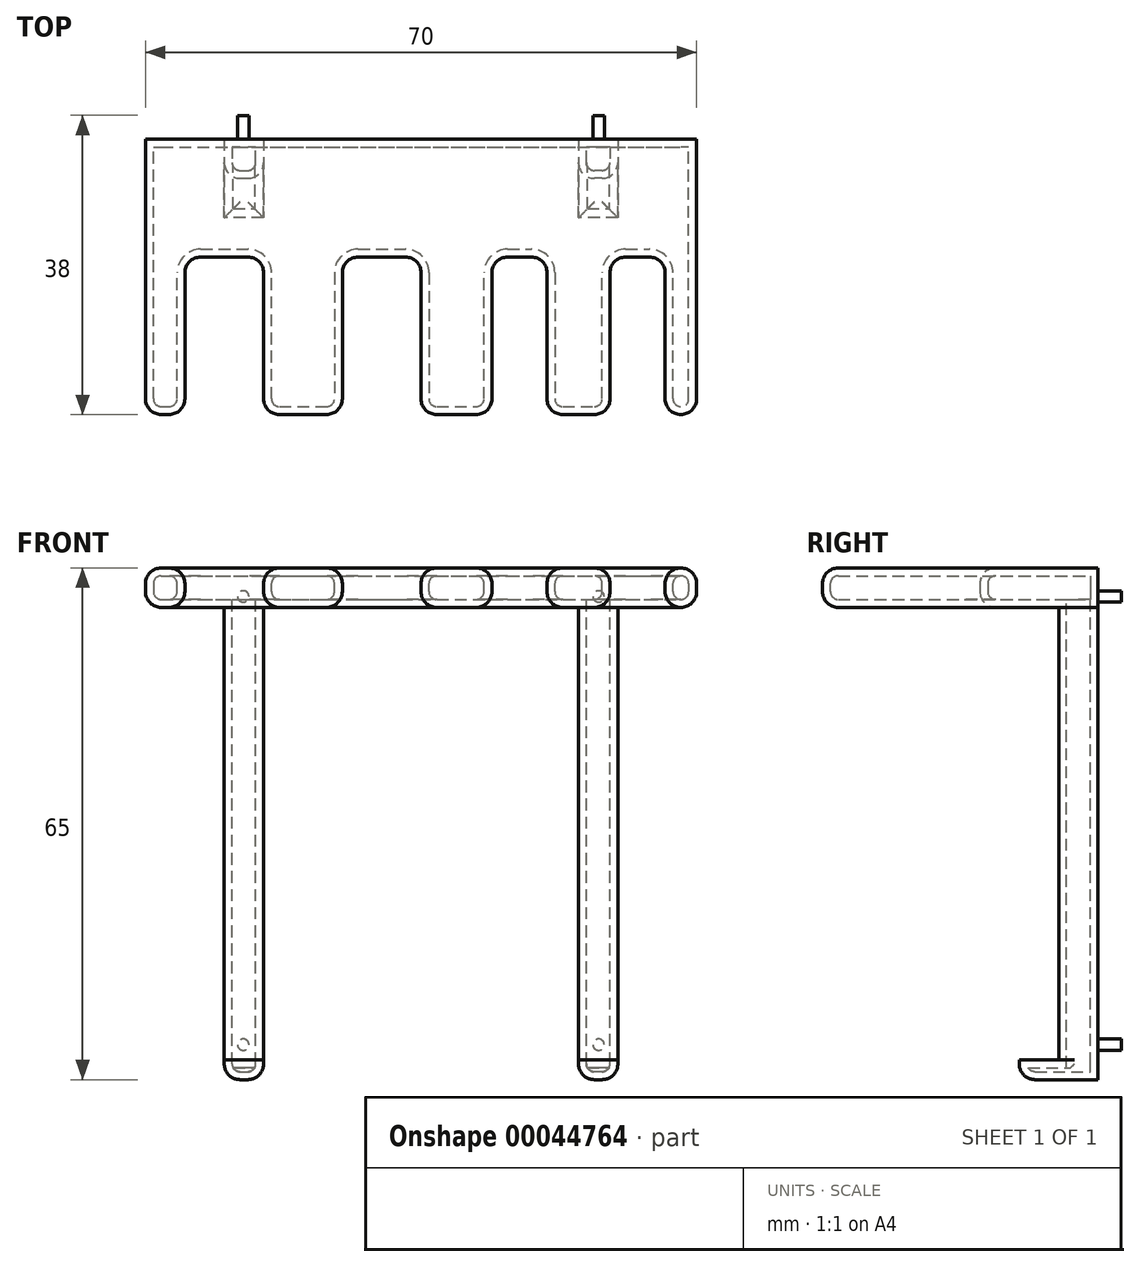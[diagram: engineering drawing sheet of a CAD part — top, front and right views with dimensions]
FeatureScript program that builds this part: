
annotation { "Feature Type Name" : "Feature", "Feature Type Description" : "" }
export const myFeature = defineFeature(function(context is Context, id is Id, definition is map)
    precondition{}
    {
        {
            var Q0;
            Q0=qCreatedBy(makeId("Top.planeOp"),FACE);
            var sketch = newSketch(context, id + "F0", { "sketchPlane" : qUnion([Q0])});
            skLineSegment(sketch, "E0.bottom", {"start": v(-35.48, -13.96) * mm, "end": v(34.52, -13.96) * mm});
            skLineSegment(sketch, "E0.left", {"start": v(-35.48, -13.96) * mm, "end": v(-35.48, -46.96) * mm});
            skLineSegment(sketch, "E0.right", {"start": v(34.52, -13.96) * mm, "end": v(34.52, -46.96) * mm});
            skLineSegment(sketch, "E1.top", {"start": v(-28.48, -28.96) * mm, "end": v(-22.48, -28.96) * mm});
            skLineSegment(sketch, "E1.left", {"start": v(-30.48, -46.96) * mm, "end": v(-30.48, -30.96) * mm});
            skLineSegment(sketch, "E1.right", {"start": v(-20.48, -46.96) * mm, "end": v(-20.48, -30.96) * mm});
            skLineSegment(sketch, "E2.top", {"start": v(-8.48, -28.96) * mm, "end": v(-2.48, -28.96) * mm});
            skLineSegment(sketch, "E2.left", {"start": v(-10.48, -46.96) * mm, "end": v(-10.48, -30.96) * mm});
            skLineSegment(sketch, "E2.right", {"start": v(-0.48, -46.96) * mm, "end": v(-0.48, -30.96) * mm});
            skLineSegment(sketch, "E3.top", {"start": v(10.52, -28.96) * mm, "end": v(13.52, -28.96) * mm});
            skLineSegment(sketch, "E3.left", {"start": v(8.52, -46.96) * mm, "end": v(8.52, -30.96) * mm});
            skLineSegment(sketch, "E3.right", {"start": v(15.52, -46.96) * mm, "end": v(15.52, -30.96) * mm});
            skLineSegment(sketch, "E4.top", {"start": v(25.52, -28.96) * mm, "end": v(28.52, -28.96) * mm});
            skLineSegment(sketch, "E4.left", {"start": v(23.52, -46.96) * mm, "end": v(23.52, -30.96) * mm});
            skLineSegment(sketch, "E4.right", {"start": v(30.52, -46.96) * mm, "end": v(30.52, -30.96) * mm});
            skLineSegment(sketch, "E5", {"start": v(-33.48, -48.96) * mm, "end": v(-32.48, -48.96) * mm});
            skLineSegment(sketch, "E6", {"start": v(-18.48, -48.96) * mm, "end": v(-12.48, -48.96) * mm});
            skLineSegment(sketch, "E7", {"start": v(1.52, -48.96) * mm, "end": v(6.52, -48.96) * mm});
            skLineSegment(sketch, "E8", {"start": v(17.52, -48.96) * mm, "end": v(21.52, -48.96) * mm});
            skLineSegment(sketch, "E9", {"start": v(32.52, -48.96) * mm, "end": v(32.52, -48.96) * mm});
            skPoint(sketch, "E10.visualSharp", {"position": v(30.52, -28.96) * mm});
            skArc(sketch, "E10.filletArc", {"start": v(30.52, -30.96) * mm, "mid": v(29.94, -29.55) * mm, "end": v(28.52, -28.96) * mm});
            skPoint(sketch, "E11.visualSharp", {"position": v(23.52, -28.96) * mm});
            skArc(sketch, "E11.filletArc", {"start": v(25.52, -28.96) * mm, "mid": v(24.1, -29.55) * mm, "end": v(23.52, -30.96) * mm});
            skPoint(sketch, "E12.visualSharp", {"position": v(15.52, -28.96) * mm});
            skArc(sketch, "E12.filletArc", {"start": v(15.52, -30.96) * mm, "mid": v(14.94, -29.55) * mm, "end": v(13.52, -28.96) * mm});
            skPoint(sketch, "E13.visualSharp", {"position": v(8.52, -28.96) * mm});
            skArc(sketch, "E13.filletArc", {"start": v(10.52, -28.96) * mm, "mid": v(9.1, -29.55) * mm, "end": v(8.52, -30.96) * mm});
            skPoint(sketch, "E14.visualSharp", {"position": v(-0.48, -28.96) * mm});
            skArc(sketch, "E14.filletArc", {"start": v(-0.48, -30.96) * mm, "mid": v(-1.06, -29.55) * mm, "end": v(-2.48, -28.96) * mm});
            skPoint(sketch, "E15.visualSharp", {"position": v(-10.48, -28.96) * mm});
            skArc(sketch, "E15.filletArc", {"start": v(-8.48, -28.96) * mm, "mid": v(-9.9, -29.55) * mm, "end": v(-10.48, -30.96) * mm});
            skPoint(sketch, "E16.visualSharp", {"position": v(-20.48, -28.96) * mm});
            skArc(sketch, "E16.filletArc", {"start": v(-20.48, -30.96) * mm, "mid": v(-21.06, -29.55) * mm, "end": v(-22.48, -28.96) * mm});
            skPoint(sketch, "E17.visualSharp", {"position": v(-30.48, -28.96) * mm});
            skArc(sketch, "E17.filletArc", {"start": v(-28.48, -28.96) * mm, "mid": v(-29.9, -29.55) * mm, "end": v(-30.48, -30.96) * mm});
            skPoint(sketch, "E18.visualSharp", {"position": v(-35.48, -48.96) * mm});
            skArc(sketch, "E18.filletArc", {"start": v(-35.48, -46.96) * mm, "mid": v(-34.9, -48.38) * mm, "end": v(-33.48, -48.96) * mm});
            skPoint(sketch, "E19.visualSharp", {"position": v(-30.48, -48.96) * mm});
            skArc(sketch, "E19.filletArc", {"start": v(-32.48, -48.96) * mm, "mid": v(-31.06, -48.38) * mm, "end": v(-30.48, -46.96) * mm});
            skPoint(sketch, "E20.visualSharp", {"position": v(-20.48, -48.96) * mm});
            skArc(sketch, "E20.filletArc", {"start": v(-20.48, -46.96) * mm, "mid": v(-19.9, -48.38) * mm, "end": v(-18.48, -48.96) * mm});
            skPoint(sketch, "E21.visualSharp", {"position": v(-10.48, -48.96) * mm});
            skArc(sketch, "E21.filletArc", {"start": v(-12.48, -48.96) * mm, "mid": v(-11.06, -48.38) * mm, "end": v(-10.48, -46.96) * mm});
            skPoint(sketch, "E22.visualSharp", {"position": v(-0.48, -48.96) * mm});
            skArc(sketch, "E22.filletArc", {"start": v(-0.48, -46.96) * mm, "mid": v(0.1, -48.38) * mm, "end": v(1.52, -48.96) * mm});
            skPoint(sketch, "E23.visualSharp", {"position": v(8.52, -48.96) * mm});
            skArc(sketch, "E23.filletArc", {"start": v(6.52, -48.96) * mm, "mid": v(7.94, -48.38) * mm, "end": v(8.52, -46.96) * mm});
            skPoint(sketch, "E24.visualSharp", {"position": v(15.52, -48.96) * mm});
            skArc(sketch, "E24.filletArc", {"start": v(15.52, -46.96) * mm, "mid": v(16.1, -48.38) * mm, "end": v(17.52, -48.96) * mm});
            skPoint(sketch, "E25.visualSharp", {"position": v(23.52, -48.96) * mm});
            skArc(sketch, "E25.filletArc", {"start": v(21.52, -48.96) * mm, "mid": v(22.94, -48.38) * mm, "end": v(23.52, -46.96) * mm});
            skPoint(sketch, "E26.visualSharp", {"position": v(30.52, -48.96) * mm});
            skArc(sketch, "E26.filletArc", {"start": v(30.52, -46.96) * mm, "mid": v(31.1, -48.38) * mm, "end": v(32.52, -48.96) * mm});
            skPoint(sketch, "E27.visualSharp", {"position": v(34.52, -48.96) * mm});
            skArc(sketch, "E27.filletArc", {"start": v(32.52, -48.96) * mm, "mid": v(33.94, -48.38) * mm, "end": v(34.52, -46.96) * mm});
            skSolve(sketch);
        }
        {
            var Q0;
            Q0=makeQuery(id+"F0.imprint","IMPRINT",FACE,{"disambiguationData":[TD([[makeQuery(id+"F0.imprint","IMPRINT",EDGE,{"derivedFrom":sQuery(id+"F0.wireOp",EDGE,"E0.bottom")}),-1.0]])]});
            extrude(context, id + "F1", {"entities" : qUnion([Q0]), "depth" : 5 * mm});
        }
        {
            var Q0;
            Q0=qCreatedBy(makeId("Top.planeOp"),FACE);
            var sketch = newSketch(context, id + "F2", { "sketchPlane" : qUnion([Q0])});
            skLineSegment(sketch, "E28.bottom", {"start": v(24.52, -13.96) * mm, "end": v(19.52, -13.96) * mm});
            skLineSegment(sketch, "E28.top", {"start": v(24.52, -18.96) * mm, "end": v(19.52, -18.96) * mm});
            skLineSegment(sketch, "E28.left", {"start": v(24.52, -13.96) * mm, "end": v(24.52, -18.96) * mm});
            skLineSegment(sketch, "E28.right", {"start": v(19.52, -13.96) * mm, "end": v(19.52, -18.96) * mm});
            skLineSegment(sketch, "E29.bottom", {"start": v(-25.48, -13.96) * mm, "end": v(-20.48, -13.96) * mm});
            skLineSegment(sketch, "E29.top", {"start": v(-25.48, -18.96) * mm, "end": v(-20.48, -18.96) * mm});
            skLineSegment(sketch, "E29.left", {"start": v(-25.48, -13.96) * mm, "end": v(-25.48, -18.96) * mm});
            skLineSegment(sketch, "E29.right", {"start": v(-20.48, -13.96) * mm, "end": v(-20.48, -18.96) * mm});
            skSolve(sketch);
        }
        {
            var Q0;
            Q0 = qSketchRegion(id + "F2", true);
            extrude(context, id + "F3", {"entities" : qUnion([Q0]), "operationType" : NewBodyOperationType.ADD, "oppositeDirection" : true, "depth" : 60 * mm});
        }
        {
            var Q0;
            Q0=makeQuery(id+"F3.opExtrude","SWEPT_FACE",FACE,{"disambiguationData":[OSD([sQuery(id+"F2.wireOp",EDGE,"E28.top")])]});
            var sketch = newSketch(context, id + "F4", { "sketchPlane" : qUnion([Q0])});
            skLineSegment(sketch, "E30.bottom", {"start": v(24.52, -60) * mm, "end": v(19.52, -60) * mm});
            skLineSegment(sketch, "E30.top", {"start": v(24.52, -57.5) * mm, "end": v(19.52, -57.5) * mm});
            skLineSegment(sketch, "E30.left", {"start": v(24.52, -60) * mm, "end": v(24.52, -57.5) * mm});
            skLineSegment(sketch, "E30.right", {"start": v(19.52, -60) * mm, "end": v(19.52, -57.5) * mm});
            skLineSegment(sketch, "E31.bottom", {"start": v(-20.48, -60) * mm, "end": v(-25.48, -60) * mm});
            skLineSegment(sketch, "E31.top", {"start": v(-20.48, -57.5) * mm, "end": v(-25.48, -57.5) * mm});
            skLineSegment(sketch, "E31.left", {"start": v(-20.48, -60) * mm, "end": v(-20.48, -57.5) * mm});
            skLineSegment(sketch, "E31.right", {"start": v(-25.48, -60) * mm, "end": v(-25.48, -57.5) * mm});
            skSolve(sketch);
        }
        {
            var Q0;
            Q0 = qSketchRegion(id + "F4", true);
            extrude(context, id + "F5", {"entities" : qUnion([Q0]), "operationType" : NewBodyOperationType.ADD, "depth" : 5 * mm});
        }
        {
            var Q0;
            Q0=makeQuery(id+"F1.opExtrude","CAP_EDGE",EDGE,{"disambiguationData":[OSD([sQuery(id+"F0.wireOp",EDGE,"E0.right")])],"isStart":true});
            var Q1;
            Q1=makeQuery(id+"F1.opExtrude","CAP_EDGE",EDGE,{"disambiguationData":[OSD([sQuery(id+"F0.wireOp",EDGE,"E0.right")])],"isStart":false});
            fillet(context, id + "F6", {"entities" : qUnion([Q0, Q1]), "radius" : 2 * mm, "tangentPropagation" : true, "allowEdgeOverflow" : false});
        }
        {
            var Q0;
            Q0=makeQuery(id+"F3.opExtrude","SWEPT_EDGE",EDGE,{"disambiguationData":[OSD([sQuery(id+"F2.wireOp",EDGE,"E28.top"),sQuery(id+"F2.wireOp",EDGE,"E28.right")])]});
            var Q1;
            Q1=makeQuery(id+"F3.opExtrude","SWEPT_EDGE",EDGE,{"disambiguationData":[OSD([sQuery(id+"F2.wireOp",EDGE,"E28.top"),sQuery(id+"F2.wireOp",EDGE,"E28.left")])]});
            var Q2;
            Q2=makeQuery(id+"F3.opExtrude","CAP_EDGE",EDGE,{"disambiguationData":[OSD([sQuery(id+"F2.wireOp",EDGE,"E28.top")])],"isStart":true});
            var Q3;
            Q3=makeQuery(id+"F3.opExtrude","SWEPT_EDGE",EDGE,{"disambiguationData":[OSD([sQuery(id+"F2.wireOp",EDGE,"E29.top"),sQuery(id+"F2.wireOp",EDGE,"E29.left")])]});
            var Q4;
            Q4=makeQuery(id+"F3.opExtrude","SWEPT_EDGE",EDGE,{"disambiguationData":[OSD([sQuery(id+"F2.wireOp",EDGE,"E29.top"),sQuery(id+"F2.wireOp",EDGE,"E29.right")])]});
            var Q5;
            Q5=makeQuery(id+"F3.opExtrude","CAP_EDGE",EDGE,{"disambiguationData":[OSD([sQuery(id+"F2.wireOp",EDGE,"E29.top")])],"isStart":true});
            var Q6;
            Q6=makeQuery(id+"F5.opExtrude","CAP_EDGE",EDGE,{"disambiguationData":[OSD([sQuery(id+"F4.wireOp",EDGE,"E30.bottom")])],"isStart":false});
            var Q7;
            Q7=makeQuery(id+"F5.boolean.opBoolean","MERGE",EDGE,{"derivedFrom":[makeQuery(id+"F3.opExtrude","CAP_EDGE",EDGE,{"disambiguationData":[OSD([sQuery(id+"F2.wireOp",EDGE,"E28.left")])],"isStart":false}),makeQuery(id+"F5.opExtrude","SWEPT_EDGE",EDGE,{"disambiguationData":[OSD([sQuery(id+"F4.wireOp",EDGE,"E30.bottom"),sQuery(id+"F4.wireOp",EDGE,"E30.left")])]})]});
            var Q8;
            Q8=makeQuery(id+"F5.boolean.opBoolean","MERGE",EDGE,{"derivedFrom":[makeQuery(id+"F3.opExtrude","CAP_EDGE",EDGE,{"disambiguationData":[OSD([sQuery(id+"F2.wireOp",EDGE,"E28.right")])],"isStart":false}),makeQuery(id+"F5.opExtrude","SWEPT_EDGE",EDGE,{"disambiguationData":[OSD([sQuery(id+"F4.wireOp",EDGE,"E30.bottom"),sQuery(id+"F4.wireOp",EDGE,"E30.right")])]})]});
            var Q9;
            Q9=makeQuery(id+"F5.opExtrude","CAP_EDGE",EDGE,{"disambiguationData":[OSD([sQuery(id+"F4.wireOp",EDGE,"E31.bottom")])],"isStart":false});
            var Q10;
            Q10=makeQuery(id+"F5.boolean.opBoolean","MERGE",EDGE,{"derivedFrom":[makeQuery(id+"F3.opExtrude","CAP_EDGE",EDGE,{"disambiguationData":[OSD([sQuery(id+"F2.wireOp",EDGE,"E29.right")])],"isStart":false}),makeQuery(id+"F5.opExtrude","SWEPT_EDGE",EDGE,{"disambiguationData":[OSD([sQuery(id+"F4.wireOp",EDGE,"E31.bottom"),sQuery(id+"F4.wireOp",EDGE,"E31.left")])]})]});
            var Q11;
            Q11=makeQuery(id+"F5.boolean.opBoolean","MERGE",EDGE,{"derivedFrom":[makeQuery(id+"F3.opExtrude","CAP_EDGE",EDGE,{"disambiguationData":[OSD([sQuery(id+"F2.wireOp",EDGE,"E29.left")])],"isStart":false}),makeQuery(id+"F5.opExtrude","SWEPT_EDGE",EDGE,{"disambiguationData":[OSD([sQuery(id+"F4.wireOp",EDGE,"E31.bottom"),sQuery(id+"F4.wireOp",EDGE,"E31.right")])]})]});
            fillet(context, id + "F7", {"entities" : qUnion([Q0, Q1, Q2, Q3, Q4, Q5, Q6, Q7, Q8, Q9, Q10, Q11]), "radius" : 2 * mm, "tangentPropagation" : true, "allowEdgeOverflow" : false});
        }
        {
            var Q0;
            Q0=makeQuery(id+"F3.boolean.opBoolean","MERGE",FACE,{"derivedFrom":[makeQuery(id+"F1.opExtrude","SWEPT_FACE",FACE,{"disambiguationData":[OSD([sQuery(id+"F0.wireOp",EDGE,"E0.bottom")])]}),makeQuery(id+"F3.opExtrude","SWEPT_FACE",FACE,{"disambiguationData":[OSD([sQuery(id+"F2.wireOp",EDGE,"E28.bottom")])]}),makeQuery(id+"F3.opExtrude","SWEPT_FACE",FACE,{"disambiguationData":[OSD([sQuery(id+"F2.wireOp",EDGE,"E29.bottom")])]})]});
            var sketch = newSketch(context, id + "F8", { "sketchPlane" : qUnion([Q0])});
            skCircle(sketch, "E32", {"center": v(23.06, 1.39) * mm, "radius": 0.72 * mm});
            skCircle(sketch, "E33", {"center": v(-22.08, 1.39) * mm, "radius": 0.72 * mm});
            skCircle(sketch, "E34", {"center": v(23.06, -55.55) * mm, "radius": 0.72 * mm});
            skCircle(sketch, "E35", {"center": v(-22.08, -55.55) * mm, "radius": 0.72 * mm});
            skSolve(sketch);
        }
        {
            var Q0;
            Q0 = qSketchRegion(id + "F8", true);
            extrude(context, id + "F9", {"entities" : qUnion([Q0]), "depth" : 3 * mm});
        }
        {
            var Q0;
            Q0=makeQuery(id+"F1.opExtrude","CAP_FACE",FACE,{"disambiguationData":[OSD([sQuery(id+"F0.wireOp",EDGE,"E0.bottom"),sQuery(id+"F0.wireOp",EDGE,"E0.left"),sQuery(id+"F0.wireOp",EDGE,"E0.right"),sQuery(id+"F0.wireOp",EDGE,"E1.top"),sQuery(id+"F0.wireOp",EDGE,"E1.left"),sQuery(id+"F0.wireOp",EDGE,"E1.right"),sQuery(id+"F0.wireOp",EDGE,"E2.top"),sQuery(id+"F0.wireOp",EDGE,"E2.left"),sQuery(id+"F0.wireOp",EDGE,"E2.right"),sQuery(id+"F0.wireOp",EDGE,"E3.top"),sQuery(id+"F0.wireOp",EDGE,"E3.left"),sQuery(id+"F0.wireOp",EDGE,"E3.right"),sQuery(id+"F0.wireOp",EDGE,"E4.top"),sQuery(id+"F0.wireOp",EDGE,"E4.left"),sQuery(id+"F0.wireOp",EDGE,"E4.right"),sQuery(id+"F0.wireOp",EDGE,"E5"),sQuery(id+"F0.wireOp",EDGE,"E6"),sQuery(id+"F0.wireOp",EDGE,"E7"),sQuery(id+"F0.wireOp",EDGE,"E8"),sQuery(id+"F0.wireOp",EDGE,"E10.filletArc"),sQuery(id+"F0.wireOp",EDGE,"E11.filletArc"),sQuery(id+"F0.wireOp",EDGE,"E12.filletArc"),sQuery(id+"F0.wireOp",EDGE,"E13.filletArc"),sQuery(id+"F0.wireOp",EDGE,"E14.filletArc"),sQuery(id+"F0.wireOp",EDGE,"E15.filletArc"),sQuery(id+"F0.wireOp",EDGE,"E16.filletArc"),sQuery(id+"F0.wireOp",EDGE,"E17.filletArc"),sQuery(id+"F0.wireOp",EDGE,"E18.filletArc"),sQuery(id+"F0.wireOp",EDGE,"E19.filletArc"),sQuery(id+"F0.wireOp",EDGE,"E20.filletArc"),sQuery(id+"F0.wireOp",EDGE,"E21.filletArc"),sQuery(id+"F0.wireOp",EDGE,"E22.filletArc"),sQuery(id+"F0.wireOp",EDGE,"E23.filletArc"),sQuery(id+"F0.wireOp",EDGE,"E24.filletArc"),sQuery(id+"F0.wireOp",EDGE,"E25.filletArc"),sQuery(id+"F0.wireOp",EDGE,"E26.filletArc"),sQuery(id+"F0.wireOp",EDGE,"E27.filletArc")])],"isStart":true});
            var Q1;
            Q1=makeQuery(id+"F1.opExtrude","SWEPT_BODY",BODY,{"disambiguationData":[OSD([sQuery(id+"F0.wireOp",EDGE,"E0.bottom"),sQuery(id+"F0.wireOp",EDGE,"E0.left"),sQuery(id+"F0.wireOp",EDGE,"E0.right"),sQuery(id+"F0.wireOp",EDGE,"E1.top"),sQuery(id+"F0.wireOp",EDGE,"E1.left"),sQuery(id+"F0.wireOp",EDGE,"E1.right"),sQuery(id+"F0.wireOp",EDGE,"E2.top"),sQuery(id+"F0.wireOp",EDGE,"E2.left"),sQuery(id+"F0.wireOp",EDGE,"E2.right"),sQuery(id+"F0.wireOp",EDGE,"E3.top"),sQuery(id+"F0.wireOp",EDGE,"E3.left"),sQuery(id+"F0.wireOp",EDGE,"E3.right"),sQuery(id+"F0.wireOp",EDGE,"E4.top"),sQuery(id+"F0.wireOp",EDGE,"E4.left"),sQuery(id+"F0.wireOp",EDGE,"E4.right"),sQuery(id+"F0.wireOp",EDGE,"E5"),sQuery(id+"F0.wireOp",EDGE,"E6"),sQuery(id+"F0.wireOp",EDGE,"E7"),sQuery(id+"F0.wireOp",EDGE,"E8"),sQuery(id+"F0.wireOp",EDGE,"E10.filletArc"),sQuery(id+"F0.wireOp",EDGE,"E11.filletArc"),sQuery(id+"F0.wireOp",EDGE,"E12.filletArc"),sQuery(id+"F0.wireOp",EDGE,"E13.filletArc"),sQuery(id+"F0.wireOp",EDGE,"E14.filletArc"),sQuery(id+"F0.wireOp",EDGE,"E15.filletArc"),sQuery(id+"F0.wireOp",EDGE,"E16.filletArc"),sQuery(id+"F0.wireOp",EDGE,"E17.filletArc"),sQuery(id+"F0.wireOp",EDGE,"E18.filletArc"),sQuery(id+"F0.wireOp",EDGE,"E19.filletArc"),sQuery(id+"F0.wireOp",EDGE,"E20.filletArc"),sQuery(id+"F0.wireOp",EDGE,"E21.filletArc"),sQuery(id+"F0.wireOp",EDGE,"E22.filletArc"),sQuery(id+"F0.wireOp",EDGE,"E23.filletArc"),sQuery(id+"F0.wireOp",EDGE,"E24.filletArc"),sQuery(id+"F0.wireOp",EDGE,"E25.filletArc"),sQuery(id+"F0.wireOp",EDGE,"E26.filletArc"),sQuery(id+"F0.wireOp",EDGE,"E27.filletArc")])]});
            shell(context, id + "F10", {"isHollow" : true, "entities" : qUnion([Q0]), "parts" : qUnion([Q1]), "thickness" : 1 * mm});
        }
    });
